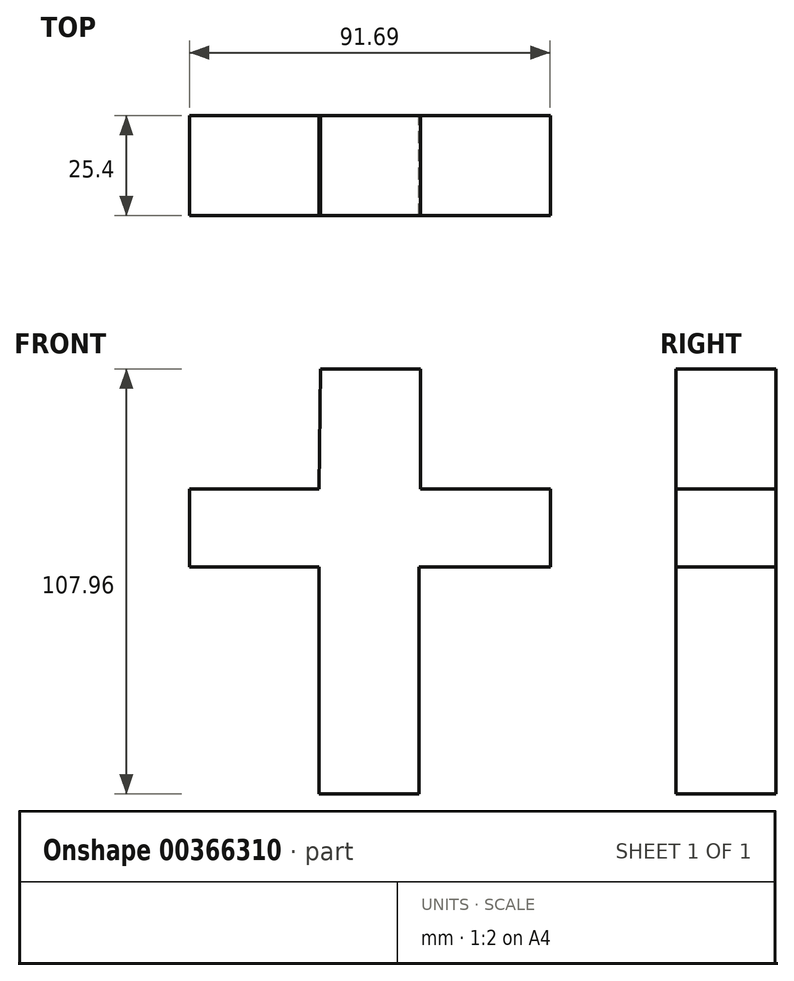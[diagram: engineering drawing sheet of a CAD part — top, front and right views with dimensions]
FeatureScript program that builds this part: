
annotation { "Feature Type Name" : "Feature", "Feature Type Description" : "" }
export const myFeature = defineFeature(function(context is Context, id is Id, definition is map)
    precondition{}
    {
        {
            var Q0;
            Q0=qCreatedBy(makeId("Front.planeOp"),FACE);
            var sketch = newSketch(context, id + "F0", { "sketchPlane" : qUnion([Q0])});
            skLineSegment(sketch, "E0", {"start": v(-25.15, 50.24) * mm, "end": v(0.25, 50.24) * mm});
            skLineSegment(sketch, "E1", {"start": v(0.25, 50.24) * mm, "end": v(0.25, 19.81) * mm});
            skLineSegment(sketch, "E2", {"start": v(0.25, 19.81) * mm, "end": v(33.27, 19.81) * mm});
            skLineSegment(sketch, "E3", {"start": v(33.27, 19.81) * mm, "end": v(33.27, 0) * mm});
            skLineSegment(sketch, "E4", {"start": v(33.27, 0) * mm, "end": v(0, 0) * mm});
            skLineSegment(sketch, "E5", {"start": v(0, 0) * mm, "end": v(0, -57.72) * mm});
            skLineSegment(sketch, "E6", {"start": v(0, -57.72) * mm, "end": v(-25.4, -57.72) * mm});
            skLineSegment(sketch, "E7", {"start": v(-25.4, -57.72) * mm, "end": v(-25.4, 0) * mm});
            skLineSegment(sketch, "E8", {"start": v(-25.4, 0) * mm, "end": v(-58.42, 0) * mm});
            skLineSegment(sketch, "E9", {"start": v(-58.42, 0) * mm, "end": v(-58.42, 19.81) * mm});
            skLineSegment(sketch, "E10", {"start": v(-58.42, 19.81) * mm, "end": v(-25.4, 19.81) * mm});
            skLineSegment(sketch, "E11", {"start": v(-25.4, 19.81) * mm, "end": v(-25.15, 50.24) * mm});
            skSolve(sketch);
        }
        {
            var Q0;
            Q0 = qSketchRegion(id + "F0", true);
            extrude(context, id + "F1", {"entities" : qUnion([Q0]), "depth" : 25.4 * mm});
        }
    });
